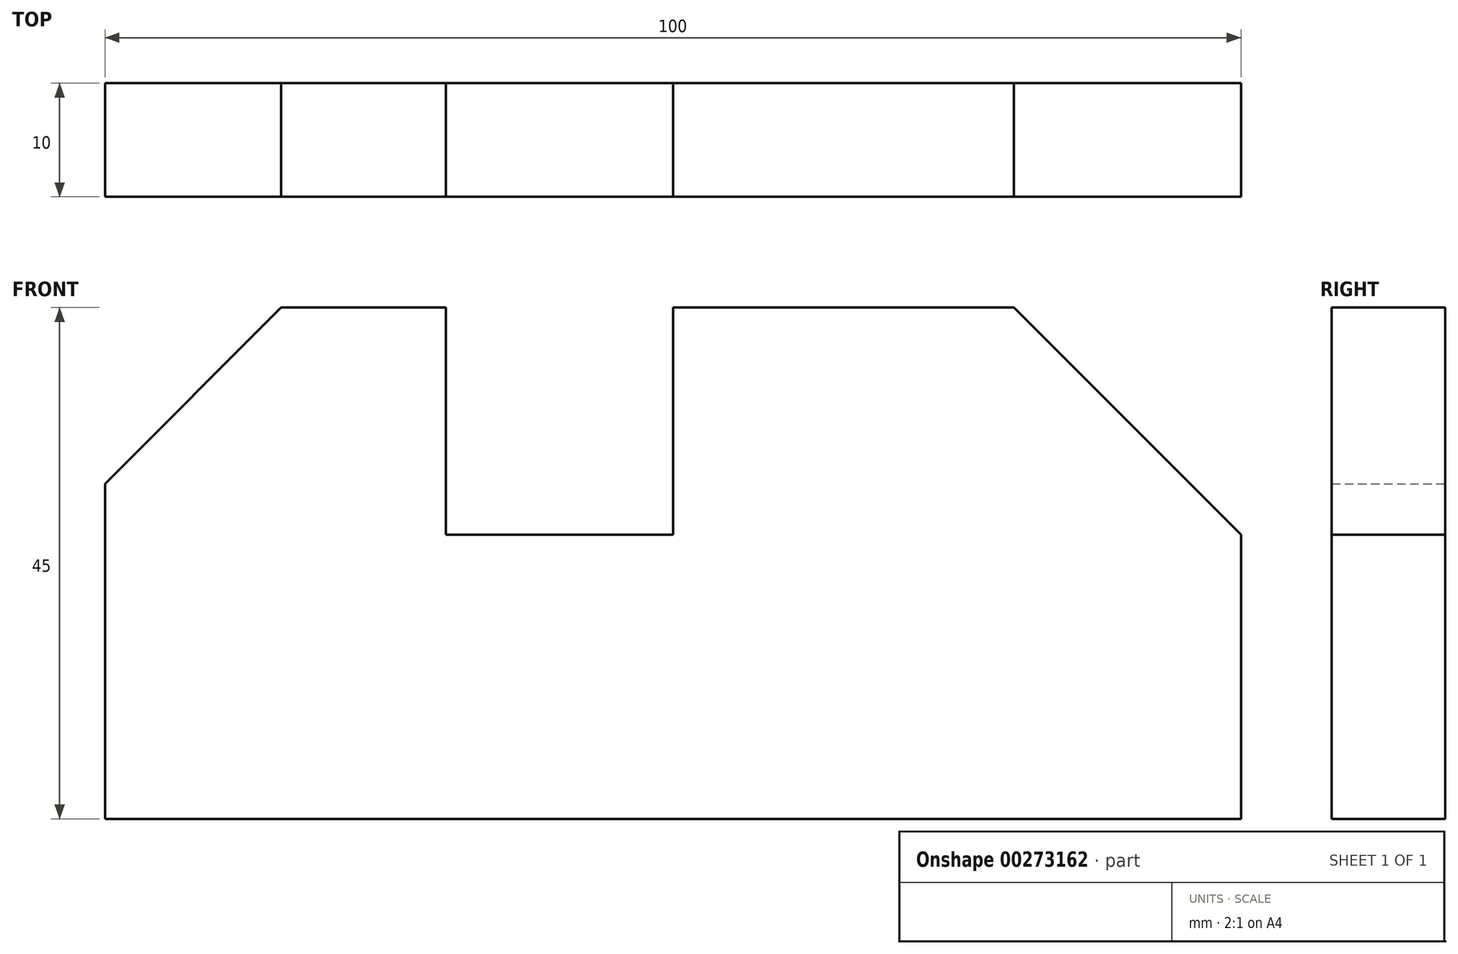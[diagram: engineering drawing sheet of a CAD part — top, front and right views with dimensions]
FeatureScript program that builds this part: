
annotation { "Feature Type Name" : "Feature", "Feature Type Description" : "" }
export const myFeature = defineFeature(function(context is Context, id is Id, definition is map)
    precondition{}
    {
        {
            var Q0;
            Q0=qCreatedBy(makeId("Front.planeOp"),FACE);
            var sketch = newSketch(context, id + "F0", { "sketchPlane" : qUnion([Q0])});
            skLineSegment(sketch, "E0", {"start": v(0, 0) * mm, "end": v(100, 0) * mm});
            skLineSegment(sketch, "E1", {"start": v(100, 0) * mm, "end": v(100, 25) * mm});
            skLineSegment(sketch, "E2", {"start": v(100, 25) * mm, "end": v(80, 45) * mm});
            skLineSegment(sketch, "E3", {"start": v(80, 45) * mm, "end": v(57.6, 45) * mm});
            skLineSegment(sketch, "E4", {"start": v(0, 0) * mm, "end": v(0, 29.49) * mm});
            skLineSegment(sketch, "E5", {"start": v(0, 29.49) * mm, "end": v(15.51, 45) * mm});
            skLineSegment(sketch, "E6", {"start": v(15.51, 45) * mm, "end": v(30, 45) * mm});
            skLineSegment(sketch, "E7", {"start": v(30, 45) * mm, "end": v(30, 25) * mm});
            skLineSegment(sketch, "E8", {"start": v(30, 25) * mm, "end": v(50, 25) * mm});
            skLineSegment(sketch, "E9", {"start": v(50, 25) * mm, "end": v(50, 45) * mm});
            skLineSegment(sketch, "E10", {"start": v(50, 45) * mm, "end": v(57.6, 45) * mm});
            skSolve(sketch);
        }
        {
            var Q0;
            Q0 = qSketchRegion(id + "F0", true);
            extrude(context, id + "F1", {"entities" : qUnion([Q0]), "depth" : 10 * mm});
        }
    });
